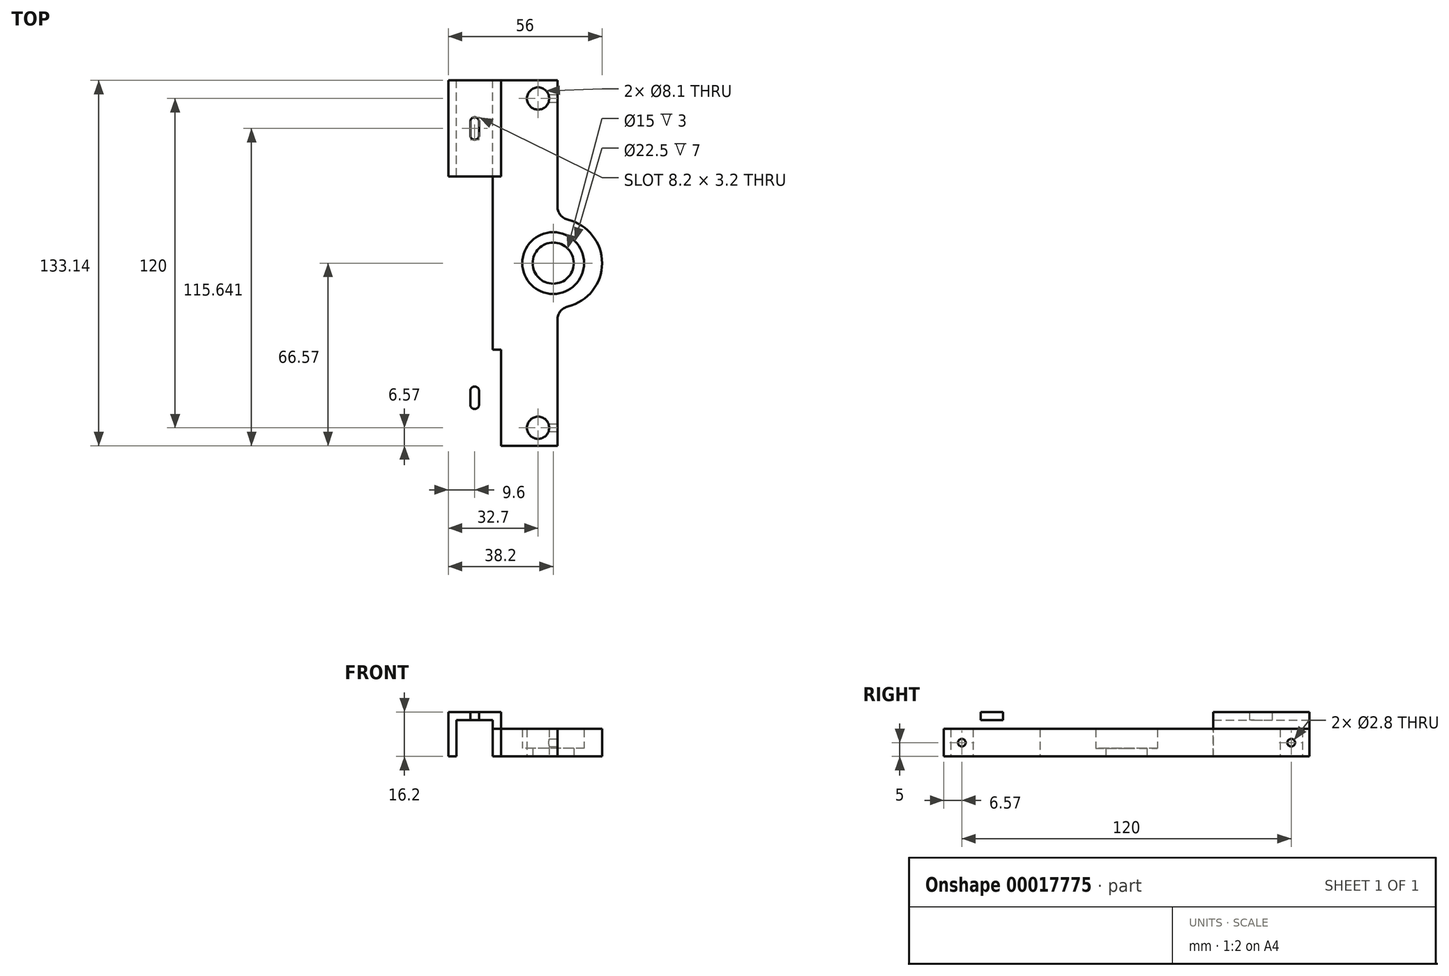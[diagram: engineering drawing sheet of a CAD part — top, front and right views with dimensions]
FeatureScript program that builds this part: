
annotation { "Feature Type Name" : "Feature", "Feature Type Description" : "" }
export const myFeature = defineFeature(function(context is Context, id is Id, definition is map)
    precondition{}
    {
        {
            var Q0;
            Q0=qCreatedBy(makeId("Top.planeOp"),FACE);
            var sketch = newSketch(context, id + "F0", { "sketchPlane" : qUnion([Q0])});
            skCircle(sketch, "E0", {"center": v(0, 0) * mm, "radius": 7.5 * mm});
            skLineSegment(sketch, "E1.rect.bottom", {"start": v(-22, -66.57) * mm, "end": v(22, -66.57) * mm});
            skLineSegment(sketch, "E1.rect.top", {"start": v(-22, 66.57) * mm, "end": v(22, 66.57) * mm});
            skLineSegment(sketch, "E1.rect.left", {"start": v(-22, -66.57) * mm, "end": v(-22, 66.57) * mm});
            skLineSegment(sketch, "E1.rect.right", {"start": v(22, -66.57) * mm, "end": v(22, 66.57) * mm});
            skCircle(sketch, "E2", {"center": v(0, 0) * mm, "radius": 11.25 * mm});
            skCircle(sketch, "E3", {"center": v(-5.5, -60) * mm, "radius": 4.05 * mm});
            skCircle(sketch, "E4", {"center": v(-5.5, 60) * mm, "radius": 4.05 * mm});
            skSolve(sketch);
        }
        {
            var Q0;
            Q0=makeQuery(id+"F0.imprint","IMPRINT",FACE,{"disambiguationData":[TD([[makeQuery(id+"F0.imprint","IMPRINT",EDGE,{"derivedFrom":sQuery(id+"F0.wireOp",EDGE,"E0")}),-1.0]])]});
            extrude(context, id + "F1", {"entities" : qUnion([Q0]), "depth" : 3 * mm});
        }
        {
            var Q0;
            Q0=makeQuery(id+"F0.imprint","IMPRINT",FACE,{"disambiguationData":[TD([[makeQuery(id+"F0.imprint","IMPRINT",EDGE,{"derivedFrom":sQuery(id+"F0.wireOp",EDGE,"E1.rect.bottom")}),1.0]])]});
            extrude(context, id + "F2", {"entities" : qUnion([Q0]), "operationType" : NewBodyOperationType.ADD, "depth" : 10 * mm});
        }
        {
            var Q0;
            Q0=makeQuery(id+"F2.opExtrude","CAP_FACE",FACE,{"disambiguationData":[OSD([sQuery(id+"F0.wireOp",EDGE,"E1.rect.bottom"),sQuery(id+"F0.wireOp",EDGE,"E1.rect.top"),sQuery(id+"F0.wireOp",EDGE,"E1.rect.left"),sQuery(id+"F0.wireOp",EDGE,"E1.rect.right"),sQuery(id+"F0.wireOp",EDGE,"E2"),sQuery(id+"F0.wireOp",EDGE,"E3"),sQuery(id+"F0.wireOp",EDGE,"E4")])],"isStart":false});
            var sketch = newSketch(context, id + "F3", { "sketchPlane" : qUnion([Q0])});
            skLineSegment(sketch, "E5", {"start": v(1.55, -66.57) * mm, "end": v(1.55, -16.25) * mm});
            skLineSegment(sketch, "E6", {"start": v(1.55, -16.25) * mm, "end": v(22, -16.25) * mm});
            skLineSegment(sketch, "E7", {"start": v(1.55, 66.57) * mm, "end": v(1.55, 16.25) * mm});
            skLineSegment(sketch, "E8", {"start": v(1.55, 16.25) * mm, "end": v(22, 16.25) * mm});
            skSolve(sketch);
        }
        {
            var Q0;
            {var subQ4=sQuery(id+"F3.wireOp",EDGE,"E5");Q0=makeQuery(id+"F3.imprint","IMPRINT",FACE,{"disambiguationData":[TD([[makeQuery(id+"F3.imprint","IMPRINT",EDGE,{"derivedFrom":subQ4}),-1.0]])]});}
            var Q1;
            {var subQ4=sQuery(id+"F3.wireOp",EDGE,"E7");Q1=makeQuery(id+"F3.imprint","IMPRINT",FACE,{"disambiguationData":[TD([[makeQuery(id+"F3.imprint","IMPRINT",EDGE,{"derivedFrom":subQ4}),1.0]])]});}
            extrude(context, id + "F4", {"entities" : qUnion([Q0, Q1]), "operationType" : NewBodyOperationType.REMOVE, "endBound" : BoundingType.UP_TO_NEXT, "oppositeDirection" : true, "depth" : 25 * mm});
        }
        {
            var Q0;
            Q0=makeQuery(id+"F2.opExtrude","CAP_FACE",FACE,{"disambiguationData":[OSD([sQuery(id+"F0.wireOp",EDGE,"E1.rect.bottom"),sQuery(id+"F0.wireOp",EDGE,"E1.rect.top"),sQuery(id+"F0.wireOp",EDGE,"E1.rect.left"),sQuery(id+"F0.wireOp",EDGE,"E1.rect.right"),sQuery(id+"F0.wireOp",EDGE,"E2"),sQuery(id+"F0.wireOp",EDGE,"E3"),sQuery(id+"F0.wireOp",EDGE,"E4")])],"isStart":false});
            var sketch = newSketch(context, id + "F5", { "sketchPlane" : qUnion([Q0])});
            skArc(sketch, "E9", {"start": v(1.55, -16.25) * mm, "mid": v(17.8, 0) * mm, "end": v(1.55, 16.25) * mm});
            skSolve(sketch);
        }
        {
            var Q0;
            Q0=makeQuery(id+"F5.imprint","IMPRINT",FACE,{"disambiguationData":[TD([[makeQuery(id+"F5.imprint","IMPRINT",EDGE,{"derivedFrom":sQuery(id+"F5.wireOp",EDGE,"E9")}),-1.0]])]});
            extrude(context, id + "F6", {"entities" : qUnion([Q0]), "operationType" : NewBodyOperationType.REMOVE, "endBound" : BoundingType.UP_TO_NEXT, "oppositeDirection" : true, "depth" : 25 * mm});
        }
        {
            var Q0;
            Q0=makeQuery(id+"F2.opExtrude","SWEPT_FACE",FACE,{"disambiguationData":[OSD([sQuery(id+"F0.wireOp",EDGE,"E1.rect.bottom")])]});
            var sketch = newSketch(context, id + "F7", { "sketchPlane" : qUnion([Q0])});
            skLineSegment(sketch, "E10", {"start": v(-22, 0) * mm, "end": v(-22, 0) * mm});
            skLineSegment(sketch, "E11", {"start": v(-22, 13.2) * mm, "end": v(-22, 0) * mm});
            skLineSegment(sketch, "E12", {"start": v(-22, 13.2) * mm, "end": v(-35.2, 13.2) * mm});
            skLineSegment(sketch, "E13", {"start": v(-35.2, 0) * mm, "end": v(-35.2, 13.2) * mm});
            skLineSegment(sketch, "E14", {"start": v(-35.2, 0) * mm, "end": v(-38.2, 0) * mm});
            skLineSegment(sketch, "E15", {"start": v(-38.2, 0) * mm, "end": v(-38.2, 16.2) * mm});
            skLineSegment(sketch, "E16", {"start": v(-22, 10) * mm, "end": v(-19, 10) * mm});
            skLineSegment(sketch, "E17", {"start": v(-19, 10) * mm, "end": v(-19, 16.2) * mm});
            skLineSegment(sketch, "E18", {"start": v(-19, 16.2) * mm, "end": v(-38.2, 16.2) * mm});
            skSolve(sketch);
        }
        {
            var Q0;
            Q0=qSketchRegion(id+"F7",true);
            var Q1;
            Q1=makeQuery(id+"F7.imprint","IMPRINT",FACE,{"disambiguationData":[TD([[makeQuery(id+"F7.imprint","IMPRINT",EDGE,{"derivedFrom":sQuery(id+"F7.wireOp",EDGE,"E10")}),-1.0]])]});
            var Q2;
            Q2=makeQuery(id+"F2.opExtrude","SWEPT_FACE",FACE,{"disambiguationData":[OSD([sQuery(id+"F0.wireOp",EDGE,"E1.rect.top")])]});
            extrude(context, id + "F8", {"entities" : qUnion([Q0, Q1]), "operationType" : NewBodyOperationType.ADD, "oppositeDirection" : true, "endBoundEntityFace" : qUnion([Q2]), "depth" : 35 * mm});
        }
        {
            var Q0;
            Q0=makeQuery(id+"F4.boolean.opBoolean","COPY",FACE,{"derivedFrom":makeQuery(id+"F4.opExtrude","SWEPT_FACE",FACE,{"disambiguationData":[OSD([sQuery(id+"F3.wireOp",EDGE,"E5")])]})});
            var sketch = newSketch(context, id + "F9", { "sketchPlane" : qUnion([Q0])});
            skCircle(sketch, "E19", {"center": v(-60, 5) * mm, "radius": 1.4 * mm});
            skPoint(sketch, "E19.centerSnap0", {"position": v(-66.57, 5) * mm});
            skCircle(sketch, "E20", {"center": v(60, 5) * mm, "radius": 1.4 * mm});
            skSolve(sketch);
        }
        {
            var Q0;
            Q0=makeQuery(id+"F9.imprint","IMPRINT",FACE,{"disambiguationData":[TD([[makeQuery(id+"F9.imprint","IMPRINT",EDGE,{"derivedFrom":sQuery(id+"F9.wireOp",EDGE,"E19")}),1.0]])]});
            var Q1;
            Q1=makeQuery(id+"F9.imprint","IMPRINT",FACE,{"disambiguationData":[TD([[makeQuery(id+"F9.imprint","IMPRINT",EDGE,{"derivedFrom":sQuery(id+"F9.wireOp",EDGE,"E20")}),1.0]])]});
            var Q2;
            Q2=makeQuery(id+"F1.opExtrude","SWEPT_BODY",BODY,{"disambiguationData":[OSD([sQuery(id+"F0.wireOp",EDGE,"E0"),sQuery(id+"F0.wireOp",EDGE,"E2")])]});
            extrude(context, id + "F10", {"entities" : qUnion([Q0, Q1]), "operationType" : NewBodyOperationType.REMOVE, "endBound" : BoundingType.UP_TO_BODY, "oppositeDirection" : true, "endBoundEntityBody" : qUnion([Q2]), "depth" : 25 * mm});
        }
        {
            var Q0;
            Q0=makeQuery(id+"F4.boolean.opBoolean","COPY",EDGE,{"derivedFrom":makeQuery(id+"F4.opExtrude","SWEPT_EDGE",EDGE,{"disambiguationData":[OSD([sQuery(id+"F0.wireOp",EDGE,"E1.rect.top"),sQuery(id+"F3.wireOp",EDGE,"E7")])]})});
            var Q1;
            Q1=makeQuery(id+"F4.boolean.opBoolean","COPY",EDGE,{"derivedFrom":makeQuery(id+"F4.opExtrude","SWEPT_EDGE",EDGE,{"disambiguationData":[OSD([sQuery(id+"F0.wireOp",EDGE,"E1.rect.bottom"),sQuery(id+"F3.wireOp",EDGE,"E5")])]})});
            var Q2;
            {var subQ0=sQuery(id+"F3.wireOp",EDGE,"E5");var subQ1=sQuery(id+"F3.wireOp",EDGE,"E6");Q2=makeQuery(id+"F6.boolean.opBoolean","MERGE",EDGE,{"derivedFrom":[makeQuery(id+"F4.boolean.opBoolean","COPY",EDGE,{"derivedFrom":makeQuery(id+"F4.opExtrude","SWEPT_EDGE",EDGE,{"disambiguationData":[OSD([subQ0,subQ1])]})}),makeQuery(id+"F6.opExtrude","SWEPT_EDGE",EDGE,{"disambiguationData":[OSD([subQ0,subQ1,sQuery(id+"F5.wireOp",EDGE,"E9")])]})]});}
            var Q3;
            {var subQ0=sQuery(id+"F3.wireOp",EDGE,"E7");var subQ1=sQuery(id+"F3.wireOp",EDGE,"E8");Q3=makeQuery(id+"F6.boolean.opBoolean","MERGE",EDGE,{"derivedFrom":[makeQuery(id+"F4.boolean.opBoolean","COPY",EDGE,{"derivedFrom":makeQuery(id+"F4.opExtrude","SWEPT_EDGE",EDGE,{"disambiguationData":[OSD([subQ0,subQ1])]})}),makeQuery(id+"F6.opExtrude","SWEPT_EDGE",EDGE,{"disambiguationData":[OSD([sQuery(id+"F0.wireOp",EDGE,"E0"),sQuery(id+"F0.wireOp",EDGE,"E1.rect.bottom"),sQuery(id+"F0.wireOp",EDGE,"E1.rect.top"),sQuery(id+"F0.wireOp",EDGE,"E1.rect.left"),sQuery(id+"F0.wireOp",EDGE,"E1.rect.right"),sQuery(id+"F0.wireOp",EDGE,"E2"),sQuery(id+"F0.wireOp",EDGE,"E3"),sQuery(id+"F0.wireOp",EDGE,"E4"),subQ0,subQ1])]})]});}
            fillet(context, id + "F11", {"entities" : qUnion([Q0, Q1, Q2, Q3]), "radius" : 5 * mm, "tangentPropagation" : true, "allowEdgeOverflow" : false});
        }
        {
            var Q0;
            Q0=makeQuery(id+"F2.opExtrude","SWEPT_FACE",FACE,{"disambiguationData":[OSD([sQuery(id+"F0.wireOp",EDGE,"E1.rect.top")])]});
            var sketch = newSketch(context, id + "F12", { "sketchPlane" : qUnion([Q0])});
            skLineSegment(sketch, "E21.0.3", {"start": v(19, 10) * mm, "end": v(19, 16.2) * mm});
            skLineSegment(sketch, "E21.0.4", {"start": v(19, 16.2) * mm, "end": v(38.2, 16.2) * mm});
            skLineSegment(sketch, "E21.0.5", {"start": v(38.2, 16.2) * mm, "end": v(38.2, 0) * mm});
            skLineSegment(sketch, "E21.0.6", {"start": v(38.2, 0) * mm, "end": v(35.2, 0) * mm});
            skLineSegment(sketch, "E21.0.7", {"start": v(35.2, 0) * mm, "end": v(35.2, 13.2) * mm});
            skLineSegment(sketch, "E21.0.8", {"start": v(35.2, 13.2) * mm, "end": v(22, 13.2) * mm});
            skLineSegment(sketch, "E22", {"start": v(19, 10) * mm, "end": v(22, 10) * mm});
            skLineSegment(sketch, "E23", {"start": v(22, 10) * mm, "end": v(22, 13.2) * mm});
            skSolve(sketch);
        }
        {
            var Q0;
            Q0 = qSketchRegion(id + "F12", true);
            var Q1;
            {var subQ1=sQuery(id+"F12.wireOp",EDGE,"E21.0.3");Q1=makeQuery(id+"F12.imprint","IMPRINT",FACE,{"disambiguationData":[TD([[makeQuery(id+"F12.imprint","IMPRINT",EDGE,{"derivedFrom":subQ1}),-1.0]])]});}
            extrude(context, id + "F13", {"entities" : qUnion([Q0, Q1]), "operationType" : NewBodyOperationType.ADD, "oppositeDirection" : true, "depth" : 35 * mm});
        }
        {
            var Q0;
            Q0=makeQuery(id+"F8.opExtrude","SWEPT_FACE",FACE,{"disambiguationData":[OSD([sQuery(id+"F7.wireOp",EDGE,"E18")])]});
            var sketch = newSketch(context, id + "F14", { "sketchPlane" : qUnion([Q0])});
            skArc(sketch, "E24.0.startCap", {"start": v(-30.2, -46.57) * mm, "mid": v(-28.6, -44.97) * mm, "end": v(-27, -46.57) * mm});
            skArc(sketch, "E24.0.endCap", {"start": v(-27, -51.57) * mm, "mid": v(-28.6, -53.17) * mm, "end": v(-30.2, -51.57) * mm});
            skLineSegment(sketch, "E24.0.left", {"start": v(-27, -46.57) * mm, "end": v(-27, -51.57) * mm});
            skLineSegment(sketch, "E24.0.right", {"start": v(-30.2, -46.57) * mm, "end": v(-30.2, -51.57) * mm});
            skArc(sketch, "E25.MirrorCS", {"start": v(-30.2, 46.57) * mm, "mid": v(-28.6, 44.97) * mm, "end": v(-27, 46.57) * mm});
            skLineSegment(sketch, "E26.MirrorCS", {"start": v(-27, 46.57) * mm, "end": v(-27, 51.57) * mm});
            skLineSegment(sketch, "E27.MirrorCS", {"start": v(-30.2, 46.57) * mm, "end": v(-30.2, 51.57) * mm});
            skArc(sketch, "E28.MirrorCS", {"start": v(-27, 51.57) * mm, "mid": v(-28.6, 53.17) * mm, "end": v(-30.2, 51.57) * mm});
            skSolve(sketch);
        }
        {
            var Q0;
            Q0=makeQuery(id+"F14.imprint","IMPRINT",FACE,{"disambiguationData":[TD([[makeQuery(id+"F14.imprint","IMPRINT",EDGE,{"derivedFrom":sQuery(id+"F14.wireOp",EDGE,"E24.0.startCap")}),-1.0]])]});
            var Q1;
            Q1=makeQuery(id+"F14.imprint","IMPRINT",FACE,{"disambiguationData":[TD([[makeQuery(id+"F14.imprint","IMPRINT",EDGE,{"derivedFrom":sQuery(id+"F14.wireOp",EDGE,"E25.MirrorCS")}),1.0]])]});
            extrude(context, id + "F15", {"entities" : qUnion([Q0, Q1]), "operationType" : NewBodyOperationType.REMOVE, "oppositeDirection" : true, "depth" : 25 * mm});
        }
    });
